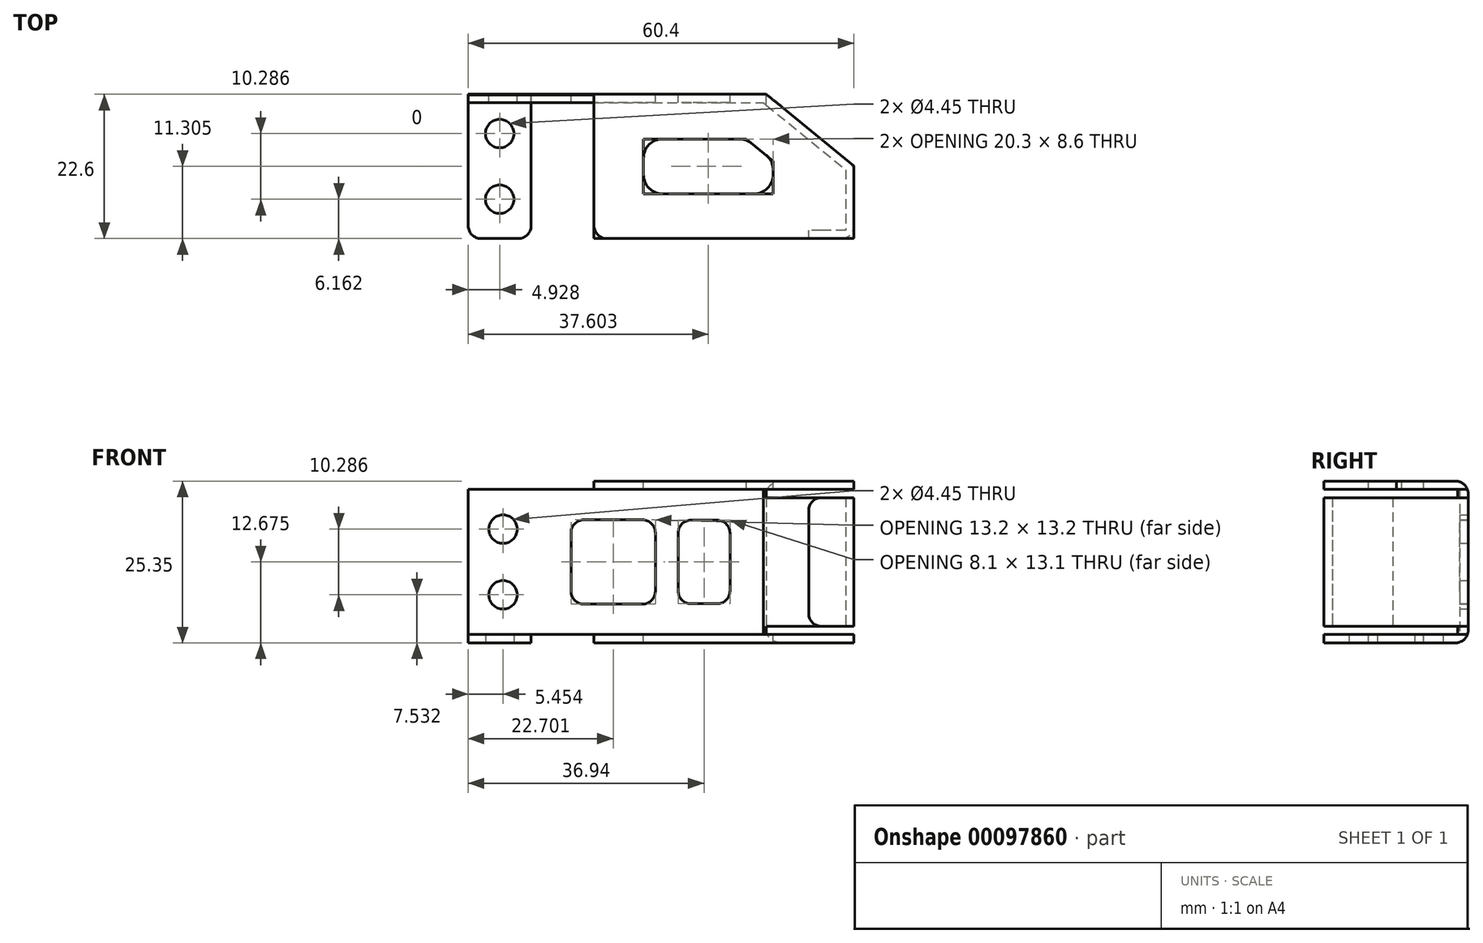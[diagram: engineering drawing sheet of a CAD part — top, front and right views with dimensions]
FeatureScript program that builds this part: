
annotation { "Feature Type Name" : "Feature", "Feature Type Description" : "" }
export const myFeature = defineFeature(function(context is Context, id is Id, definition is map)
    precondition{}
    {
        {
            var Q0;
            Q0=qCreatedBy(makeId("Top.planeOp"),FACE);
            var sketch = newSketch(context, id + "F0", { "sketchPlane" : qUnion([Q0])});
            skLineSegment(sketch, "E0.bottom", {"start": v(-31.59, -12.14) * mm, "end": v(13.31, -12.14) * mm});
            skLineSegment(sketch, "E0.top", {"start": v(-31.59, -33.44) * mm, "end": v(26.21, -33.44) * mm});
            skLineSegment(sketch, "E0.left", {"start": v(-31.59, -12.14) * mm, "end": v(-31.59, -33.44) * mm});
            skLineSegment(sketch, "E0.right", {"start": v(26.21, -22.66) * mm, "end": v(26.21, -33.44) * mm});
            skLineSegment(sketch, "E1", {"start": v(13.31, -12.14) * mm, "end": v(26.21, -22.66) * mm});
            skSolve(sketch);
        }
        {
            var Q0;
            Q0=makeQuery(id+"F0.imprint","IMPRINT",FACE,{"disambiguationData":[TD([[makeQuery(id+"F0.imprint","IMPRINT",EDGE,{"derivedFrom":sQuery(id+"F0.wireOp",EDGE,"E0.bottom")}),-1.0]])]});
            extrude(context, id + "F1", {"entities" : qUnion([Q0]), "depth" : 22.75 * mm});
        }
        {
            var Q0;
            Q0=makeQuery(id+"F1.opExtrude","SWEPT_FACE",FACE,{"disambiguationData":[OSD([sQuery(id+"F0.wireOp",EDGE,"E0.top")])]});
            shell(context, id + "F2", {"entities" : qUnion([Q0]), "thickness" : 1.3 * mm, "oppositeDirection" : true});
        }
        {
            var Q0;
            Q0=makeQuery(id+"F1.opExtrude","SWEPT_FACE",FACE,{"disambiguationData":[OSD([sQuery(id+"F0.wireOp",EDGE,"E0.left")])]});
            var sketch = newSketch(context, id + "F3", { "sketchPlane" : qUnion([Q0])});
            skLineSegment(sketch, "E2", {"start": v(12.14, -1.3) * mm, "end": v(12.14, 22.75) * mm});
            skLineSegment(sketch, "E3", {"start": v(12.14, 22.75) * mm, "end": v(33.44, 22.75) * mm});
            skSolve(sketch);
        }
        {
            var Q0;
            {var subQ0=sQuery(id+"F3.wireOp",EDGE,"E2");Q0=makeQuery(id+"F3.imprint","IMPRINT",FACE,{"disambiguationData":[TD([[makeQuery(id+"F3.imprint","IMPRINT",EDGE,{"derivedFrom":subQ0}),-1.0]])]});}
            extrude(context, id + "F4", {"entities" : qUnion([Q0]), "operationType" : NewBodyOperationType.REMOVE, "oppositeDirection" : true, "depth" : 19.7 * mm});
        }
        {
            var Q0;
            Q0=makeQuery(id+"F1.opExtrude","CAP_FACE",FACE,{"disambiguationData":[OSD([sQuery(id+"F0.wireOp",EDGE,"E0.bottom"),sQuery(id+"F0.wireOp",EDGE,"E0.top"),sQuery(id+"F0.wireOp",EDGE,"E0.left"),sQuery(id+"F0.wireOp",EDGE,"E0.right"),sQuery(id+"F0.wireOp",EDGE,"E1")])],"isStart":false});
            var sketch = newSketch(context, id + "F5", { "sketchPlane" : qUnion([Q0])});
            skLineSegment(sketch, "E4", {"start": v(-13.19, -12.14) * mm, "end": v(-13.19, -33.44) * mm});
            skLineSegment(sketch, "E5", {"start": v(-23.04, -33.44) * mm, "end": v(-23.04, -12.14) * mm});
            skLineSegment(sketch, "E6", {"start": v(-13.19, -33.44) * mm, "end": v(-32.89, -33.44) * mm});
            skLineSegment(sketch, "E7", {"start": v(-32.89, -33.44) * mm, "end": v(-23.04, -33.44) * mm});
            skLineSegment(sketch, "E8", {"start": v(-23.04, -12.14) * mm, "end": v(-32.89, -12.14) * mm});
            skLineSegment(sketch, "E9", {"start": v(-23.04, -12.14) * mm, "end": v(-23.04, -10.84) * mm});
            skLineSegment(sketch, "E10", {"start": v(-13.19, -12.14) * mm, "end": v(-13.19, -10.84) * mm});
            skSolve(sketch);
        }
        {
            var Q0;
            Q0=makeQuery(id+"F5.imprint","IMPRINT",FACE,{"disambiguationData":[TD([[makeQuery(id+"F5.imprint","IMPRINT",EDGE,{"derivedFrom":sQuery(id+"F5.wireOp",EDGE,"E4")}),-1.0]])]});
            extrude(context, id + "F6", {"entities" : qUnion([Q0]), "operationType" : NewBodyOperationType.REMOVE, "oppositeDirection" : true, "depth" : 1.3 * mm});
        }
        {
            var Q0;
            {var subQ0=sQuery(id+"F0.wireOp",EDGE,"E1");var subQ1=sQuery(id+"F0.wireOp",EDGE,"E0.top");var subQ2=sQuery(id+"F0.wireOp",EDGE,"E0.right");var subQ3=sQuery(id+"F0.wireOp",EDGE,"E0.bottom");Q0=makeQuery(id+"F6.boolean.opBoolean","SPLIT",FACE,{"disambiguationData":[TD([makeQuery(id+"F1.opExtrude","SWEPT_FACE",FACE,{"disambiguationData":[OSD([subQ2])]})])],"derivedFrom":makeQuery(id+"F1.opExtrude","CAP_FACE",FACE,{"disambiguationData":[OSD([subQ3,subQ1,sQuery(id+"F0.wireOp",EDGE,"E0.left"),subQ2,subQ0])],"isStart":false})});}
            var sketch = newSketch(context, id + "F7", { "sketchPlane" : qUnion([Q0])});
            skLineSegment(sketch, "E11", {"start": v(-5.44, -17.84) * mm, "end": v(10.65, -17.84) * mm});
            skLineSegment(sketch, "E12", {"start": v(10.65, -17.84) * mm, "end": v(14.86, -21.27) * mm});
            skLineSegment(sketch, "E13", {"start": v(14.86, -21.27) * mm, "end": v(14.86, -26.44) * mm});
            skLineSegment(sketch, "E14", {"start": v(14.86, -26.44) * mm, "end": v(-5.44, -26.44) * mm});
            skLineSegment(sketch, "E15", {"start": v(-5.44, -26.44) * mm, "end": v(-5.44, -17.84) * mm});
            skSolve(sketch);
        }
        {
            var Q0;
            Q0=makeQuery(id+"F7.imprint","IMPRINT",FACE,{"disambiguationData":[TD([[makeQuery(id+"F7.imprint","IMPRINT",EDGE,{"derivedFrom":sQuery(id+"F7.wireOp",EDGE,"E11")}),-1.0]])]});
            extrude(context, id + "F8", {"entities" : qUnion([Q0]), "operationType" : NewBodyOperationType.REMOVE, "oppositeDirection" : true, "depth" : 61.35 * mm});
        }
        {
            var Q0;
            Q0=makeQuery(id+"F1.opExtrude","SWEPT_FACE",FACE,{"disambiguationData":[OSD([sQuery(id+"F0.wireOp",EDGE,"E0.bottom")])]});
            var sketch = newSketch(context, id + "F9", { "sketchPlane" : qUnion([Q0])});
            skLineSegment(sketch, "E16.bottom", {"start": v(-8.1, 4.82) * mm, "end": v(0, 4.82) * mm});
            skLineSegment(sketch, "E16.top", {"start": v(-8.1, 17.93) * mm, "end": v(0, 17.93) * mm});
            skLineSegment(sketch, "E16.left", {"start": v(-8.1, 4.82) * mm, "end": v(-8.1, 17.93) * mm});
            skLineSegment(sketch, "E16.right", {"start": v(0, 4.82) * mm, "end": v(0, 17.93) * mm});
            skLineSegment(sketch, "E17.bottom", {"start": v(3.59, 4.77) * mm, "end": v(16.79, 4.77) * mm});
            skLineSegment(sketch, "E17.top", {"start": v(3.59, 17.97) * mm, "end": v(16.79, 17.97) * mm});
            skLineSegment(sketch, "E17.left", {"start": v(3.59, 4.77) * mm, "end": v(3.59, 17.98) * mm});
            skLineSegment(sketch, "E17.right", {"start": v(16.79, 4.77) * mm, "end": v(16.79, 17.97) * mm});
            skLineSegment(sketch, "E18", {"start": v(27.44, -1.3) * mm, "end": v(27.44, 24.05) * mm, "construction": true});
            skLineSegment(sketch, "E19", {"start": v(-13.78, 11.38) * mm, "end": v(32.89, 11.38) * mm, "construction": true});
            skCircle(sketch, "E20", {"center": v(27.44, 16.52) * mm, "radius": 2.23 * mm});
            skCircle(sketch, "E21", {"center": v(27.44, 6.23) * mm, "radius": 2.23 * mm});
            skLineSegment(sketch, "E22", {"start": v(27.44, 14.3) * mm, "end": v(27.44, 11.38) * mm});
            skLineSegment(sketch, "E23", {"start": v(27.44, 11.38) * mm, "end": v(27.44, 8.46) * mm});
            skLineSegment(sketch, "E24", {"start": v(13.19, -1.3) * mm, "end": v(13.19, 0) * mm});
            skLineSegment(sketch, "E25", {"start": v(13.19, 0) * mm, "end": v(32.89, 0) * mm});
            skPoint(sketch, "E26", {"position": v(16.79, 11.37) * mm});
            skPoint(sketch, "E27", {"position": v(0, 11.37) * mm});
            skSolve(sketch);
        }
        {
            var Q0;
            Q0=makeQuery(id+"F9.imprint","IMPRINT",FACE,{"disambiguationData":[TD([[makeQuery(id+"F9.imprint","IMPRINT",EDGE,{"derivedFrom":sQuery(id+"F9.wireOp",EDGE,"E16.bottom")}),1.0]])]});
            var Q1;
            Q1=makeQuery(id+"F9.imprint","IMPRINT",FACE,{"disambiguationData":[TD([[makeQuery(id+"F9.imprint","IMPRINT",EDGE,{"derivedFrom":sQuery(id+"F9.wireOp",EDGE,"E17.bottom")}),1.0]])]});
            var Q2;
            {var subQ0=sQuery(id+"F9.wireOp",EDGE,"E24");Q2=makeQuery(id+"F9.imprint","IMPRINT",FACE,{"disambiguationData":[TD([[makeQuery(id+"F9.imprint","IMPRINT",EDGE,{"derivedFrom":subQ0}),-1.0]])]});}
            var Q3;
            Q3=makeQuery(id+"F9.imprint","IMPRINT",FACE,{"disambiguationData":[TD([[makeQuery(id+"F9.imprint","IMPRINT",EDGE,{"derivedFrom":sQuery(id+"F9.wireOp",EDGE,"E21")}),1.0]])]});
            var Q4;
            Q4=makeQuery(id+"F9.imprint","IMPRINT",FACE,{"disambiguationData":[TD([[makeQuery(id+"F9.imprint","IMPRINT",EDGE,{"derivedFrom":sQuery(id+"F9.wireOp",EDGE,"E20")}),1.0]])]});
            extrude(context, id + "F10", {"entities" : qUnion([Q0, Q1, Q2, Q3, Q4]), "operationType" : NewBodyOperationType.REMOVE, "oppositeDirection" : true, "depth" : 25 * mm});
        }
        {
            var Q0;
            Q0=makeQuery(id+"F2.opShell","OFFSET_FACE",FACE,{"disambiguationData":[OSD([sQuery(id+"F0.wireOp",EDGE,"E0.right")])]});
            var sketch = newSketch(context, id + "F11", { "sketchPlane" : qUnion([Q0])});
            skLineSegment(sketch, "E28", {"start": v(32.14, 22.75) * mm, "end": v(32.14, 0) * mm});
            skSolve(sketch);
        }
        {
            var Q0;
            {var subQ0=sQuery(id+"F11.wireOp",EDGE,"E28");Q0=makeQuery(id+"F11.imprint","IMPRINT",FACE,{"disambiguationData":[TD([[makeQuery(id+"F11.imprint","IMPRINT",EDGE,{"derivedFrom":subQ0}),1.0]])]});}
            extrude(context, id + "F12", {"entities" : qUnion([Q0]), "operationType" : NewBodyOperationType.ADD, "depth" : 5.8 * mm});
        }
        {
            var Q0;
            Q0=makeQuery(id+"F1.opExtrude","SWEPT_FACE",FACE,{"disambiguationData":[OSD([sQuery(id+"F0.wireOp",EDGE,"E0.bottom")])]});
            var sketch = newSketch(context, id + "F13", { "sketchPlane" : qUnion([Q0])});
            skLineSegment(sketch, "E29", {"start": v(-13.78, 0) * mm, "end": v(-36.67, 0) * mm});
            skLineSegment(sketch, "E30", {"start": v(-13.78, 22.75) * mm, "end": v(-38.37, 22.75) * mm});
            skLineSegment(sketch, "E31", {"start": v(-13.78, 1.3) * mm, "end": v(-36.66, 1.3) * mm});
            skLineSegment(sketch, "E32", {"start": v(-13.78, 21.45) * mm, "end": v(-38.37, 21.45) * mm});
            skLineSegment(sketch, "E33", {"start": v(-36.67, 0) * mm, "end": v(-36.66, 1.3) * mm});
            skLineSegment(sketch, "E34", {"start": v(-38.37, 21.45) * mm, "end": v(-38.37, 22.75) * mm});
            skSolve(sketch);
        }
        {
            var Q0;
            {var subQ0=sQuery(id+"F13.wireOp",EDGE,"E29");Q0=makeQuery(id+"F13.imprint","IMPRINT",FACE,{"disambiguationData":[TD([[makeQuery(id+"F13.imprint","IMPRINT",EDGE,{"derivedFrom":subQ0}),-1.0]])]});}
            var Q1;
            {var subQ0=sQuery(id+"F13.wireOp",EDGE,"E30");Q1=makeQuery(id+"F13.imprint","IMPRINT",FACE,{"disambiguationData":[TD([[makeQuery(id+"F13.imprint","IMPRINT",EDGE,{"derivedFrom":subQ0}),1.0]])]});}
            extrude(context, id + "F14", {"entities" : qUnion([Q0, Q1]), "operationType" : NewBodyOperationType.REMOVE, "oppositeDirection" : true, "depth" : 25 * mm});
        }
        {
            var Q0;
            Q0=makeQuery(id+"F4.boolean.opBoolean","COPY",EDGE,{"derivedFrom":makeQuery(id+"F4.opExtrude","CAP_EDGE",EDGE,{"disambiguationData":[OSD([sQuery(id+"F0.wireOp",EDGE,"E0.top"),sQuery(id+"F0.wireOp",EDGE,"E0.left")])],"isStart":false})});
            var Q1;
            {var subQ0=sQuery(id+"F0.wireOp",EDGE,"E0.right");var subQ1=sQuery(id+"F0.wireOp",EDGE,"E0.top");Q1=makeQuery(id+"F14.boolean.opBoolean","SPLIT",EDGE,{"disambiguationData":[TD([makeQuery(id+"F14.opExtrude","SWEPT_FACE",FACE,{"disambiguationData":[OSD([sQuery(id+"F13.wireOp",EDGE,"E31")])]})])],"derivedFrom":makeQuery(id+"F1.opExtrude","SWEPT_EDGE",EDGE,{"disambiguationData":[OSD([subQ1,subQ0])]})});}
            var Q2;
            {var subQ1=sQuery(id+"F0.wireOp",EDGE,"E0.right");var subQ3=sQuery(id+"F0.wireOp",EDGE,"E0.top");Q2=makeQuery(id+"F14.boolean.opBoolean","SPLIT",EDGE,{"disambiguationData":[TD([makeQuery(id+"F14.opExtrude","SWEPT_FACE",FACE,{"disambiguationData":[OSD([sQuery(id+"F13.wireOp",EDGE,"E29")])]})])],"derivedFrom":makeQuery(id+"F1.opExtrude","SWEPT_EDGE",EDGE,{"disambiguationData":[OSD([subQ3,subQ1])]})});}
            var Q3;
            {var subQ1=sQuery(id+"F0.wireOp",EDGE,"E0.right");var subQ3=sQuery(id+"F0.wireOp",EDGE,"E0.top");Q3=makeQuery(id+"F14.boolean.opBoolean","SPLIT",EDGE,{"disambiguationData":[TD([makeQuery(id+"F4.opExtrude","SWEPT_FACE",FACE,{"disambiguationData":[OSD([sQuery(id+"F3.wireOp",EDGE,"E3")])]})])],"derivedFrom":makeQuery(id+"F1.opExtrude","SWEPT_EDGE",EDGE,{"disambiguationData":[OSD([subQ3,subQ1])]})});}
            var Q4;
            Q4=makeQuery(id+"F6.boolean.opBoolean","COPY",EDGE,{"derivedFrom":makeQuery(id+"F6.opExtrude","SWEPT_EDGE",EDGE,{"disambiguationData":[OSD([sQuery(id+"F0.wireOp",EDGE,"E0.top"),sQuery(id+"F5.wireOp",EDGE,"E4"),sQuery(id+"F5.wireOp",EDGE,"E6")])]})});
            var Q5;
            Q5=makeQuery(id+"F1.opExtrude","SWEPT_EDGE",EDGE,{"disambiguationData":[OSD([sQuery(id+"F0.wireOp",EDGE,"E0.top"),sQuery(id+"F0.wireOp",EDGE,"E0.left")])]});
            var Q6;
            Q6=makeQuery(id+"F6.boolean.opBoolean","COPY",EDGE,{"derivedFrom":makeQuery(id+"F6.opExtrude","SWEPT_EDGE",EDGE,{"disambiguationData":[OSD([sQuery(id+"F5.wireOp",EDGE,"E5"),sQuery(id+"F5.wireOp",EDGE,"E6"),sQuery(id+"F5.wireOp",EDGE,"E7")])]})});
            var Q7;
            Q7=makeQuery(id+"F10.boolean.opBoolean","COPY",EDGE,{"derivedFrom":makeQuery(id+"F10.opExtrude","SWEPT_EDGE",EDGE,{"disambiguationData":[OSD([sQuery(id+"F0.wireOp",EDGE,"E0.bottom"),sQuery(id+"F0.wireOp",EDGE,"E0.left"),sQuery(id+"F9.wireOp",EDGE,"E25")])]})});
            var Q8;
            Q8=makeQuery(id+"F14.boolean.opBoolean","INTERSECT",EDGE,{"derivedFrom":[makeQuery(id+"F12.opExtrude","CAP_FACE",FACE,{"disambiguationData":[OSD([sQuery(id+"F0.wireOp",EDGE,"E0.top"),sQuery(id+"F0.wireOp",EDGE,"E0.right"),sQuery(id+"F11.wireOp",EDGE,"E28")])],"isStart":false}),makeQuery(id+"F14.opExtrude","SWEPT_FACE",FACE,{"disambiguationData":[OSD([sQuery(id+"F13.wireOp",EDGE,"E31")])]})]});
            var Q9;
            Q9=makeQuery(id+"F14.boolean.opBoolean","INTERSECT",EDGE,{"derivedFrom":[makeQuery(id+"F12.opExtrude","CAP_FACE",FACE,{"disambiguationData":[OSD([sQuery(id+"F0.wireOp",EDGE,"E0.top"),sQuery(id+"F0.wireOp",EDGE,"E0.right"),sQuery(id+"F11.wireOp",EDGE,"E28")])],"isStart":false}),makeQuery(id+"F14.opExtrude","SWEPT_FACE",FACE,{"disambiguationData":[OSD([sQuery(id+"F13.wireOp",EDGE,"E32")])]})]});
            fillet(context, id + "F15", {"entities" : qUnion([Q0, Q1, Q2, Q3, Q4, Q5, Q6, Q7, Q8, Q9]), "radius" : 2 * mm, "tangentPropagation" : true, "allowEdgeOverflow" : false});
        }
        {
            var Q0;
            {var subQ0=sQuery(id+"F0.wireOp",EDGE,"E1");var subQ1=sQuery(id+"F0.wireOp",EDGE,"E0.right");var subQ2=sQuery(id+"F0.wireOp",EDGE,"E0.left");var subQ3=sQuery(id+"F0.wireOp",EDGE,"E0.top");var subQ4=sQuery(id+"F0.wireOp",EDGE,"E0.bottom");var subQ5=makeQuery(id+"F1.opExtrude","CAP_FACE",FACE,{"disambiguationData":[OSD([subQ4,subQ3,subQ2,subQ1,subQ0])],"isStart":true});var subQ6=sQuery(id+"F7.wireOp",EDGE,"E13");var subQ7=sQuery(id+"F7.wireOp",EDGE,"E12");Q0=makeQuery(id+"F8.boolean.opBoolean","COPY",EDGE,{"disambiguationData":[TD([subQ5])],"derivedFrom":makeQuery(id+"F8.opExtrude","SWEPT_EDGE",EDGE,{"disambiguationData":[OSD([subQ7,subQ6])]})});}
            var Q1;
            {var subQ0=sQuery(id+"F0.wireOp",EDGE,"E1");var subQ1=sQuery(id+"F0.wireOp",EDGE,"E0.right");var subQ2=sQuery(id+"F0.wireOp",EDGE,"E0.left");var subQ3=sQuery(id+"F0.wireOp",EDGE,"E0.top");var subQ4=sQuery(id+"F0.wireOp",EDGE,"E0.bottom");var subQ5=makeQuery(id+"F1.opExtrude","CAP_FACE",FACE,{"disambiguationData":[OSD([subQ4,subQ3,subQ2,subQ1,subQ0])],"isStart":true});var subQ6=sQuery(id+"F7.wireOp",EDGE,"E11");var subQ7=sQuery(id+"F7.wireOp",EDGE,"E12");Q1=makeQuery(id+"F8.boolean.opBoolean","COPY",EDGE,{"disambiguationData":[TD([subQ5])],"derivedFrom":makeQuery(id+"F8.opExtrude","SWEPT_EDGE",EDGE,{"disambiguationData":[OSD([subQ6,subQ7])]})});}
            var Q2;
            {var subQ0=sQuery(id+"F0.wireOp",EDGE,"E1");var subQ1=sQuery(id+"F0.wireOp",EDGE,"E0.right");var subQ2=sQuery(id+"F0.wireOp",EDGE,"E0.left");var subQ3=sQuery(id+"F0.wireOp",EDGE,"E0.top");var subQ4=sQuery(id+"F0.wireOp",EDGE,"E0.bottom");var subQ5=makeQuery(id+"F1.opExtrude","CAP_FACE",FACE,{"disambiguationData":[OSD([subQ4,subQ3,subQ2,subQ1,subQ0])],"isStart":true});var subQ6=sQuery(id+"F7.wireOp",EDGE,"E11");var subQ7=sQuery(id+"F7.wireOp",EDGE,"E15");Q2=makeQuery(id+"F8.boolean.opBoolean","COPY",EDGE,{"disambiguationData":[TD([subQ5])],"derivedFrom":makeQuery(id+"F8.opExtrude","SWEPT_EDGE",EDGE,{"disambiguationData":[OSD([subQ6,subQ7])]})});}
            var Q3;
            {var subQ0=sQuery(id+"F0.wireOp",EDGE,"E1");var subQ1=sQuery(id+"F0.wireOp",EDGE,"E0.right");var subQ2=sQuery(id+"F0.wireOp",EDGE,"E0.left");var subQ3=sQuery(id+"F0.wireOp",EDGE,"E0.top");var subQ4=sQuery(id+"F0.wireOp",EDGE,"E0.bottom");var subQ5=makeQuery(id+"F1.opExtrude","CAP_FACE",FACE,{"disambiguationData":[OSD([subQ4,subQ3,subQ2,subQ1,subQ0])],"isStart":true});var subQ6=sQuery(id+"F7.wireOp",EDGE,"E14");var subQ7=sQuery(id+"F7.wireOp",EDGE,"E15");Q3=makeQuery(id+"F8.boolean.opBoolean","COPY",EDGE,{"disambiguationData":[TD([subQ5])],"derivedFrom":makeQuery(id+"F8.opExtrude","SWEPT_EDGE",EDGE,{"disambiguationData":[OSD([subQ6,subQ7])]})});}
            var Q4;
            {var subQ0=sQuery(id+"F0.wireOp",EDGE,"E1");var subQ1=sQuery(id+"F0.wireOp",EDGE,"E0.right");var subQ2=sQuery(id+"F0.wireOp",EDGE,"E0.left");var subQ3=sQuery(id+"F0.wireOp",EDGE,"E0.top");var subQ4=sQuery(id+"F0.wireOp",EDGE,"E0.bottom");var subQ5=makeQuery(id+"F1.opExtrude","CAP_FACE",FACE,{"disambiguationData":[OSD([subQ4,subQ3,subQ2,subQ1,subQ0])],"isStart":true});var subQ6=sQuery(id+"F7.wireOp",EDGE,"E13");var subQ7=sQuery(id+"F7.wireOp",EDGE,"E14");Q4=makeQuery(id+"F8.boolean.opBoolean","COPY",EDGE,{"disambiguationData":[TD([subQ5])],"derivedFrom":makeQuery(id+"F8.opExtrude","SWEPT_EDGE",EDGE,{"disambiguationData":[OSD([subQ6,subQ7])]})});}
            var Q5;
            {var subQ0=sQuery(id+"F7.wireOp",EDGE,"E11");var subQ7=sQuery(id+"F7.wireOp",EDGE,"E12");Q5=makeQuery(id+"F8.boolean.opBoolean","COPY",EDGE,{"disambiguationData":[TD([makeQuery(id+"F4.opExtrude","SWEPT_FACE",FACE,{"disambiguationData":[OSD([sQuery(id+"F3.wireOp",EDGE,"E3")])]})])],"derivedFrom":makeQuery(id+"F8.opExtrude","SWEPT_EDGE",EDGE,{"disambiguationData":[OSD([subQ0,subQ7])]})});}
            var Q6;
            {var subQ0=sQuery(id+"F7.wireOp",EDGE,"E12");var subQ7=sQuery(id+"F7.wireOp",EDGE,"E13");Q6=makeQuery(id+"F8.boolean.opBoolean","COPY",EDGE,{"disambiguationData":[TD([makeQuery(id+"F4.opExtrude","SWEPT_FACE",FACE,{"disambiguationData":[OSD([sQuery(id+"F3.wireOp",EDGE,"E3")])]})])],"derivedFrom":makeQuery(id+"F8.opExtrude","SWEPT_EDGE",EDGE,{"disambiguationData":[OSD([subQ0,subQ7])]})});}
            var Q7;
            {var subQ0=sQuery(id+"F7.wireOp",EDGE,"E13");var subQ7=sQuery(id+"F7.wireOp",EDGE,"E14");Q7=makeQuery(id+"F8.boolean.opBoolean","COPY",EDGE,{"disambiguationData":[TD([makeQuery(id+"F4.opExtrude","SWEPT_FACE",FACE,{"disambiguationData":[OSD([sQuery(id+"F3.wireOp",EDGE,"E3")])]})])],"derivedFrom":makeQuery(id+"F8.opExtrude","SWEPT_EDGE",EDGE,{"disambiguationData":[OSD([subQ0,subQ7])]})});}
            var Q8;
            {var subQ0=sQuery(id+"F7.wireOp",EDGE,"E14");var subQ7=sQuery(id+"F7.wireOp",EDGE,"E15");Q8=makeQuery(id+"F8.boolean.opBoolean","COPY",EDGE,{"disambiguationData":[TD([makeQuery(id+"F4.opExtrude","SWEPT_FACE",FACE,{"disambiguationData":[OSD([sQuery(id+"F3.wireOp",EDGE,"E3")])]})])],"derivedFrom":makeQuery(id+"F8.opExtrude","SWEPT_EDGE",EDGE,{"disambiguationData":[OSD([subQ0,subQ7])]})});}
            var Q9;
            {var subQ0=sQuery(id+"F7.wireOp",EDGE,"E11");var subQ7=sQuery(id+"F7.wireOp",EDGE,"E15");Q9=makeQuery(id+"F8.boolean.opBoolean","COPY",EDGE,{"disambiguationData":[TD([makeQuery(id+"F4.opExtrude","SWEPT_FACE",FACE,{"disambiguationData":[OSD([sQuery(id+"F3.wireOp",EDGE,"E3")])]})])],"derivedFrom":makeQuery(id+"F8.opExtrude","SWEPT_EDGE",EDGE,{"disambiguationData":[OSD([subQ0,subQ7])]})});}
            fillet(context, id + "F16", {"entities" : qUnion([Q0, Q1, Q2, Q3, Q4, Q5, Q6, Q7, Q8, Q9]), "radius" : 3 * mm, "tangentPropagation" : true, "allowEdgeOverflow" : false});
        }
        {
            var Q0;
            {var subQ0=sQuery(id+"F0.wireOp",EDGE,"E0.bottom");var subQ1=sQuery(id+"F0.wireOp",EDGE,"E1");Q0=makeQuery(id+"F6.boolean.opBoolean","SPLIT",EDGE,{"disambiguationData":[TD([makeQuery(id+"F1.opExtrude","SWEPT_FACE",FACE,{"disambiguationData":[OSD([subQ1])]})])],"derivedFrom":makeQuery(id+"F1.opExtrude","CAP_EDGE",EDGE,{"disambiguationData":[OSD([subQ0])],"isStart":false})});}
            var Q1;
            {var subQ0=sQuery(id+"F0.wireOp",EDGE,"E0.bottom");var subQ1=sQuery(id+"F0.wireOp",EDGE,"E0.left");Q1=makeQuery(id+"F6.boolean.opBoolean","SPLIT",EDGE,{"disambiguationData":[TD([makeQuery(id+"F1.opExtrude","SWEPT_FACE",FACE,{"disambiguationData":[OSD([subQ1])]})])],"derivedFrom":makeQuery(id+"F1.opExtrude","CAP_EDGE",EDGE,{"disambiguationData":[OSD([subQ0])],"isStart":false})});}
            var Q2;
            Q2=makeQuery(id+"F1.opExtrude","CAP_EDGE",EDGE,{"disambiguationData":[OSD([sQuery(id+"F0.wireOp",EDGE,"E0.bottom")])],"isStart":true});
            var Q3;
            {var subQ0=sQuery(id+"F0.wireOp",EDGE,"E0.right");var subQ1=sQuery(id+"F0.wireOp",EDGE,"E1");Q3=makeQuery(id+"F14.boolean.opBoolean","SPLIT",EDGE,{"disambiguationData":[TD([makeQuery(id+"F14.opExtrude","SWEPT_FACE",FACE,{"disambiguationData":[OSD([sQuery(id+"F13.wireOp",EDGE,"E31")])]})])],"derivedFrom":makeQuery(id+"F1.opExtrude","SWEPT_EDGE",EDGE,{"disambiguationData":[OSD([subQ0,subQ1])]})});}
            var Q4;
            {var subQ0=sQuery(id+"F0.wireOp",EDGE,"E1");var subQ1=sQuery(id+"F0.wireOp",EDGE,"E0.right");Q4=makeQuery(id+"F14.boolean.opBoolean","SPLIT",EDGE,{"disambiguationData":[TD([makeQuery(id+"F4.opExtrude","SWEPT_FACE",FACE,{"disambiguationData":[OSD([sQuery(id+"F3.wireOp",EDGE,"E3")])]})])],"derivedFrom":makeQuery(id+"F1.opExtrude","SWEPT_EDGE",EDGE,{"disambiguationData":[OSD([subQ1,subQ0])]})});}
            var Q5;
            {var subQ0=sQuery(id+"F0.wireOp",EDGE,"E1");var subQ1=sQuery(id+"F0.wireOp",EDGE,"E0.right");Q5=makeQuery(id+"F14.boolean.opBoolean","SPLIT",EDGE,{"disambiguationData":[TD([makeQuery(id+"F14.opExtrude","SWEPT_FACE",FACE,{"disambiguationData":[OSD([sQuery(id+"F13.wireOp",EDGE,"E29")])]})])],"derivedFrom":makeQuery(id+"F1.opExtrude","SWEPT_EDGE",EDGE,{"disambiguationData":[OSD([subQ1,subQ0])]})});}
            fillet(context, id + "F17", {"entities" : qUnion([Q0, Q1, Q2, Q3, Q4, Q5]), "radius" : 2 * mm, "tangentPropagation" : true, "allowEdgeOverflow" : false});
        }
        {
            var Q0;
            Q0=makeQuery(id+"F10.boolean.opBoolean","COPY",EDGE,{"derivedFrom":makeQuery(id+"F10.opExtrude","SWEPT_EDGE",EDGE,{"disambiguationData":[OSD([sQuery(id+"F9.wireOp",EDGE,"E16.top"),sQuery(id+"F9.wireOp",EDGE,"E16.right")])]})});
            var Q1;
            Q1=makeQuery(id+"F10.boolean.opBoolean","COPY",EDGE,{"derivedFrom":makeQuery(id+"F10.opExtrude","SWEPT_EDGE",EDGE,{"disambiguationData":[OSD([sQuery(id+"F9.wireOp",EDGE,"E16.bottom"),sQuery(id+"F9.wireOp",EDGE,"E16.right")])]})});
            var Q2;
            Q2=makeQuery(id+"F10.boolean.opBoolean","COPY",EDGE,{"derivedFrom":makeQuery(id+"F10.opExtrude","SWEPT_EDGE",EDGE,{"disambiguationData":[OSD([sQuery(id+"F9.wireOp",EDGE,"E16.bottom"),sQuery(id+"F9.wireOp",EDGE,"E16.left")])]})});
            var Q3;
            Q3=makeQuery(id+"F10.boolean.opBoolean","COPY",EDGE,{"derivedFrom":makeQuery(id+"F10.opExtrude","SWEPT_EDGE",EDGE,{"disambiguationData":[OSD([sQuery(id+"F9.wireOp",EDGE,"E16.top"),sQuery(id+"F9.wireOp",EDGE,"E16.left")])]})});
            var Q4;
            Q4=makeQuery(id+"F10.boolean.opBoolean","COPY",EDGE,{"derivedFrom":makeQuery(id+"F10.opExtrude","SWEPT_EDGE",EDGE,{"disambiguationData":[OSD([sQuery(id+"F9.wireOp",EDGE,"E17.bottom"),sQuery(id+"F9.wireOp",EDGE,"E17.right")])]})});
            var Q5;
            Q5=makeQuery(id+"F10.boolean.opBoolean","COPY",EDGE,{"derivedFrom":makeQuery(id+"F10.opExtrude","SWEPT_EDGE",EDGE,{"disambiguationData":[OSD([sQuery(id+"F9.wireOp",EDGE,"E17.top"),sQuery(id+"F9.wireOp",EDGE,"E17.right")])]})});
            var Q6;
            Q6=makeQuery(id+"F10.boolean.opBoolean","COPY",EDGE,{"derivedFrom":makeQuery(id+"F10.opExtrude","SWEPT_EDGE",EDGE,{"disambiguationData":[OSD([sQuery(id+"F9.wireOp",EDGE,"E17.top"),sQuery(id+"F9.wireOp",EDGE,"E17.left")])]})});
            var Q7;
            Q7=makeQuery(id+"F10.boolean.opBoolean","COPY",EDGE,{"derivedFrom":makeQuery(id+"F10.opExtrude","SWEPT_EDGE",EDGE,{"disambiguationData":[OSD([sQuery(id+"F9.wireOp",EDGE,"E17.bottom"),sQuery(id+"F9.wireOp",EDGE,"E17.left")])]})});
            fillet(context, id + "F18", {"entities" : qUnion([Q0, Q1, Q2, Q3, Q4, Q5, Q6, Q7]), "radius" : 2 * mm, "tangentPropagation" : true, "allowEdgeOverflow" : false});
        }
        {
            var Q0;
            Q0=makeQuery(id+"F1.opExtrude","CAP_FACE",FACE,{"disambiguationData":[OSD([sQuery(id+"F0.wireOp",EDGE,"E0.bottom"),sQuery(id+"F0.wireOp",EDGE,"E0.top"),sQuery(id+"F0.wireOp",EDGE,"E0.left"),sQuery(id+"F0.wireOp",EDGE,"E0.right"),sQuery(id+"F0.wireOp",EDGE,"E1")])],"isStart":true});
            var sketch = newSketch(context, id + "F19", { "sketchPlane" : qUnion([Q0])});
            skLineSegment(sketch, "E35.0", {"start": v(13.78, 10.84) * mm, "end": v(-32.4, 10.84) * mm});
            skLineSegment(sketch, "E36.0", {"start": v(-23.04, 31.44) * mm, "end": v(-23.04, 12.14) * mm});
            skArc(sketch, "E37.0", {"start": v(-23.04, 31.44) * mm, "mid": v(-23.62, 32.85) * mm, "end": v(-25.04, 33.44) * mm});
            skLineSegment(sketch, "E38.0", {"start": v(-30.89, 33.44) * mm, "end": v(-25.04, 33.44) * mm});
            skArc(sketch, "E39.0", {"start": v(-30.89, 33.44) * mm, "mid": v(-32.3, 32.85) * mm, "end": v(-32.89, 31.44) * mm});
            skLineSegment(sketch, "E40.0", {"start": v(-32.89, 12.14) * mm, "end": v(-32.89, 31.44) * mm});
            skLineSegment(sketch, "E41", {"start": v(-23.04, 12.14) * mm, "end": v(-23.04, 10.84) * mm});
            skLineSegment(sketch, "E42", {"start": v(-23.04, 10.84) * mm, "end": v(-32.89, 10.84) * mm});
            skLineSegment(sketch, "E43", {"start": v(-32.89, 10.84) * mm, "end": v(-32.89, 12.14) * mm});
            skSolve(sketch);
        }
        {
            var Q0;
            Q0 = qSketchRegion(id + "F19", true);
            extrude(context, id + "F20", {"entities" : qUnion([Q0]), "operationType" : NewBodyOperationType.ADD, "oppositeDirection" : true, "depth" : 1.3 * mm});
        }
        {
            var Q0;
            Q0=makeQuery(id+"F20.opExtrude","CAP_FACE",FACE,{"disambiguationData":[OSD([sQuery(id+"F19.wireOp",EDGE,"E36.0"),sQuery(id+"F19.wireOp",EDGE,"E37.0"),sQuery(id+"F19.wireOp",EDGE,"E38.0"),sQuery(id+"F19.wireOp",EDGE,"E39.0"),sQuery(id+"F19.wireOp",EDGE,"E40.0"),sQuery(id+"F19.wireOp",EDGE,"E41"),sQuery(id+"F19.wireOp",EDGE,"E42"),sQuery(id+"F19.wireOp",EDGE,"E43")])],"isStart":false});
            var sketch = newSketch(context, id + "F21", { "sketchPlane" : qUnion([Q0])});
            skLineSegment(sketch, "E44.0", {"start": v(-32.89, -10.84) * mm, "end": v(-32.89, -12.14) * mm});
            skLineSegment(sketch, "E45.0", {"start": v(-23.04, -12.14) * mm, "end": v(-30.89, -12.14) * mm});
            skLineSegment(sketch, "E46", {"start": v(-30.89, -12.14) * mm, "end": v(-32.89, -12.14) * mm});
            skLineSegment(sketch, "E47", {"start": v(-23.04, -12.14) * mm, "end": v(-23.04, -10.96) * mm});
            skLineSegment(sketch, "E48", {"start": v(-23.04, -10.96) * mm, "end": v(-23.04, -10.84) * mm});
            skLineSegment(sketch, "E49", {"start": v(-23.04, -10.84) * mm, "end": v(-32.89, -10.84) * mm});
            skSolve(sketch);
        }
        {
            var Q0;
            Q0 = qSketchRegion(id + "F21", true);
            extrude(context, id + "F22", {"entities" : qUnion([Q0]), "operationType" : NewBodyOperationType.ADD, "depth" : 2.5 * mm});
        }
        {
            var Q0;
            Q0=makeQuery(id+"F20.opExtrude","CAP_EDGE",EDGE,{"disambiguationData":[OSD([sQuery(id+"F19.wireOp",EDGE,"E42")])],"isStart":true});
            fillet(context, id + "F23", {"entities" : qUnion([Q0]), "radius" : 2 * mm, "tangentPropagation" : true, "allowEdgeOverflow" : false});
        }
        {
            var Q0;
            {var subQ0=sQuery(id+"F0.wireOp",EDGE,"E0.bottom");var subQ1=sQuery(id+"F0.wireOp",EDGE,"E0.top");var subQ2=sQuery(id+"F0.wireOp",EDGE,"E0.left");Q0=makeQuery(id+"F6.boolean.opBoolean","SPLIT",FACE,{"disambiguationData":[TD([makeQuery(id+"F1.opExtrude","SWEPT_FACE",FACE,{"disambiguationData":[OSD([subQ2])]})])],"derivedFrom":makeQuery(id+"F1.opExtrude","CAP_FACE",FACE,{"disambiguationData":[OSD([subQ0,subQ1,subQ2,sQuery(id+"F0.wireOp",EDGE,"E0.right"),sQuery(id+"F0.wireOp",EDGE,"E1")])],"isStart":false})});}
            var sketch = newSketch(context, id + "F24", { "sketchPlane" : qUnion([Q0])});
            skLineSegment(sketch, "E50.0", {"start": v(-13.19, -10.96) * mm, "end": v(-13.19, -12.14) * mm});
            skLineSegment(sketch, "E51.0", {"start": v(-32.89, -10.84) * mm, "end": v(-13.19, -10.84) * mm});
            skLineSegment(sketch, "E52.0", {"start": v(-32.89, -12.84) * mm, "end": v(-32.89, -31.44) * mm});
            skLineSegment(sketch, "E53.0", {"start": v(-32.89, -12.84) * mm, "end": v(-32.89, -10.84) * mm});
            skLineSegment(sketch, "E54.0", {"start": v(-13.19, -12.84) * mm, "end": v(-13.19, -10.96) * mm});
            skLineSegment(sketch, "E55.0", {"start": v(-13.19, -12.84) * mm, "end": v(-13.19, -31.44) * mm});
            skLineSegment(sketch, "E56.0", {"start": v(-30.89, -33.44) * mm, "end": v(-25.04, -33.44) * mm});
            skArc(sketch, "E57.0", {"start": v(-32.89, -31.44) * mm, "mid": v(-32.3, -32.85) * mm, "end": v(-30.89, -33.44) * mm});
            skLineSegment(sketch, "E58", {"start": v(-13.19, -33.44) * mm, "end": v(-25.04, -33.44) * mm});
            skLineSegment(sketch, "E59", {"start": v(-13.19, -31.44) * mm, "end": v(-13.19, -33.44) * mm});
            skPoint(sketch, "E60.orphan", {"position": v(-11.19, -33.44) * mm});
            skLineSegment(sketch, "E61", {"start": v(-13.19, -10.96) * mm, "end": v(-13.19, -10.84) * mm});
            skPoint(sketch, "E62.orphan", {"position": v(13.78, -10.84) * mm});
            skSolve(sketch);
        }
        {
            var Q0;
            Q0 = qSketchRegion(id + "F24", true);
            extrude(context, id + "F25", {"entities" : qUnion([Q0]), "operationType" : NewBodyOperationType.REMOVE, "oppositeDirection" : true, "depth" : 1.3 * mm});
        }
        {
            var Q0;
            Q0=makeQuery(id+"F20.opExtrude","CAP_FACE",FACE,{"disambiguationData":[OSD([sQuery(id+"F19.wireOp",EDGE,"E36.0"),sQuery(id+"F19.wireOp",EDGE,"E37.0"),sQuery(id+"F19.wireOp",EDGE,"E38.0"),sQuery(id+"F19.wireOp",EDGE,"E39.0"),sQuery(id+"F19.wireOp",EDGE,"E40.0"),sQuery(id+"F19.wireOp",EDGE,"E41"),sQuery(id+"F19.wireOp",EDGE,"E42"),sQuery(id+"F19.wireOp",EDGE,"E43")])],"isStart":true});
            var sketch = newSketch(context, id + "F26", { "sketchPlane" : qUnion([Q0])});
            skLineSegment(sketch, "E63", {"start": v(-23.04, 22.14) * mm, "end": v(-32.89, 22.14) * mm, "construction": true});
            skLineSegment(sketch, "E64", {"start": v(-27.96, 12.84) * mm, "end": v(-27.96, 33.44) * mm, "construction": true});
            skCircle(sketch, "E65", {"center": v(-27.96, 27.28) * mm, "radius": 2.23 * mm});
            skCircle(sketch, "E66", {"center": v(-27.96, 17) * mm, "radius": 2.23 * mm});
            skLineSegment(sketch, "E67", {"start": v(-27.96, 17) * mm, "end": v(-27.96, 27.28) * mm, "construction": true});
            skPoint(sketch, "E68", {"position": v(-27.96, 22.14) * mm});
            skSolve(sketch);
        }
        {
            var Q0;
            Q0 = qSketchRegion(id + "F26", true);
            extrude(context, id + "F27", {"entities" : qUnion([Q0]), "operationType" : NewBodyOperationType.REMOVE, "oppositeDirection" : true, "depth" : 25 * mm});
        }
    });
